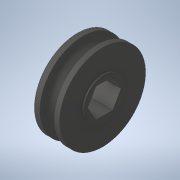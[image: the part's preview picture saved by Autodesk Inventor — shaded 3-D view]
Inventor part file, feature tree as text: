
AUTODESK INVENTOR PART (.ipt)
format: ipt  version: 2020 (Build 240168000, 168)  size: 167,936 bytes
history: native  units: in
note: dims shown in document units (in); Inventor stores cm internally (conversion verified against a paired STEP export)
features: fillet x1
ambient origin geometry x8: Origin, YZ Plane, XZ Plane, XY Plane, X Axis, Y Axis, Z Axis, Center Point
bodies: Solid1 (feature_tree)
feature tree (1):
  fillet  "Fillet1"  [1 undecoded]
note: 1 required parameter value undecoded (feature->parameter linkage not recoverable at this tier; creation-order binding heuristic only, values carry confidence <= 0.55)
